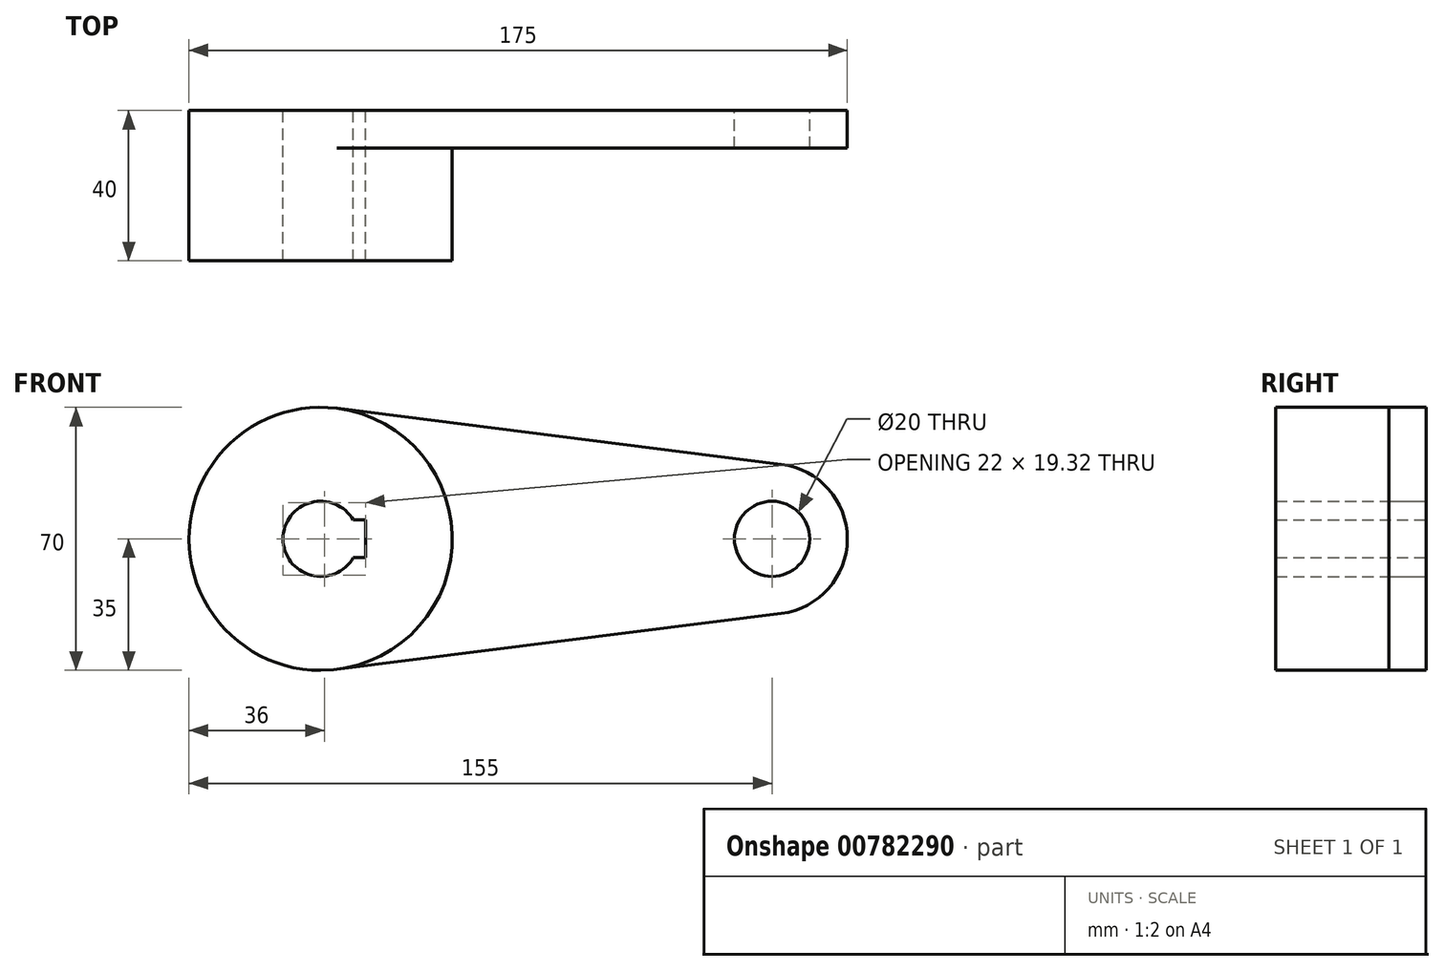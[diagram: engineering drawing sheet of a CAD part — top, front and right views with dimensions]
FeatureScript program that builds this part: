
annotation { "Feature Type Name" : "Feature", "Feature Type Description" : "" }
export const myFeature = defineFeature(function(context is Context, id is Id, definition is map)
    precondition{}
    {
        {
            var Q0;
            Q0=qCreatedBy(makeId("Front.planeOp"),FACE);
            var sketch = newSketch(context, id + "F0", { "sketchPlane" : qUnion([Q0])});
            skCircle(sketch, "E0", {"center": v(0, 0) * mm, "radius": 10 * mm});
            skCircle(sketch, "E1", {"center": v(0, 0) * mm, "radius": 20 * mm});
            skArc(sketch, "E2", {"start": v(-111.34, 5) * mm, "mid": v(-130, 0) * mm, "end": v(-111.34, -5) * mm});
            skCircle(sketch, "E3", {"center": v(-120, 0) * mm, "radius": 35 * mm});
            skLineSegment(sketch, "E4", {"start": v(-115.62, 34.73) * mm, "end": v(2.5, 19.84) * mm});
            skLineSegment(sketch, "E5", {"start": v(-115.62, -34.73) * mm, "end": v(2.5, -19.84) * mm});
            skLineSegment(sketch, "E6", {"start": v(-111.34, 5) * mm, "end": v(-108, 5) * mm});
            skLineSegment(sketch, "E7", {"start": v(-108, 5) * mm, "end": v(-108, -5) * mm});
            skLineSegment(sketch, "E8", {"start": v(-108, -5) * mm, "end": v(-111.34, -5) * mm});
            skPoint(sketch, "E9.start.orphan", {"position": v(-120, -5) * mm});
            skSolve(sketch);
        }
        {
            var Q0;
            Q0=makeQuery(id+"F0.imprint","IMPRINT",FACE,{"disambiguationData":[TD([[makeQuery(id+"F0.imprint","IMPRINT",EDGE,{"derivedFrom":sQuery(id+"F0.wireOp",EDGE,"E2")}),-1.0]])]});
            extrude(context, id + "F1", {"entities" : qUnion([Q0]), "depth" : 40 * mm, "offsetDistance" : 25.4 * mm});
        }
        {
            var Q0;
            Q0 = qSketchRegion(id + "F0", true);
            extrude(context, id + "F2", {"entities" : qUnion([Q0]), "operationType" : NewBodyOperationType.ADD, "depth" : 10 * mm, "offsetDistance" : 25.4 * mm});
        }
    });
